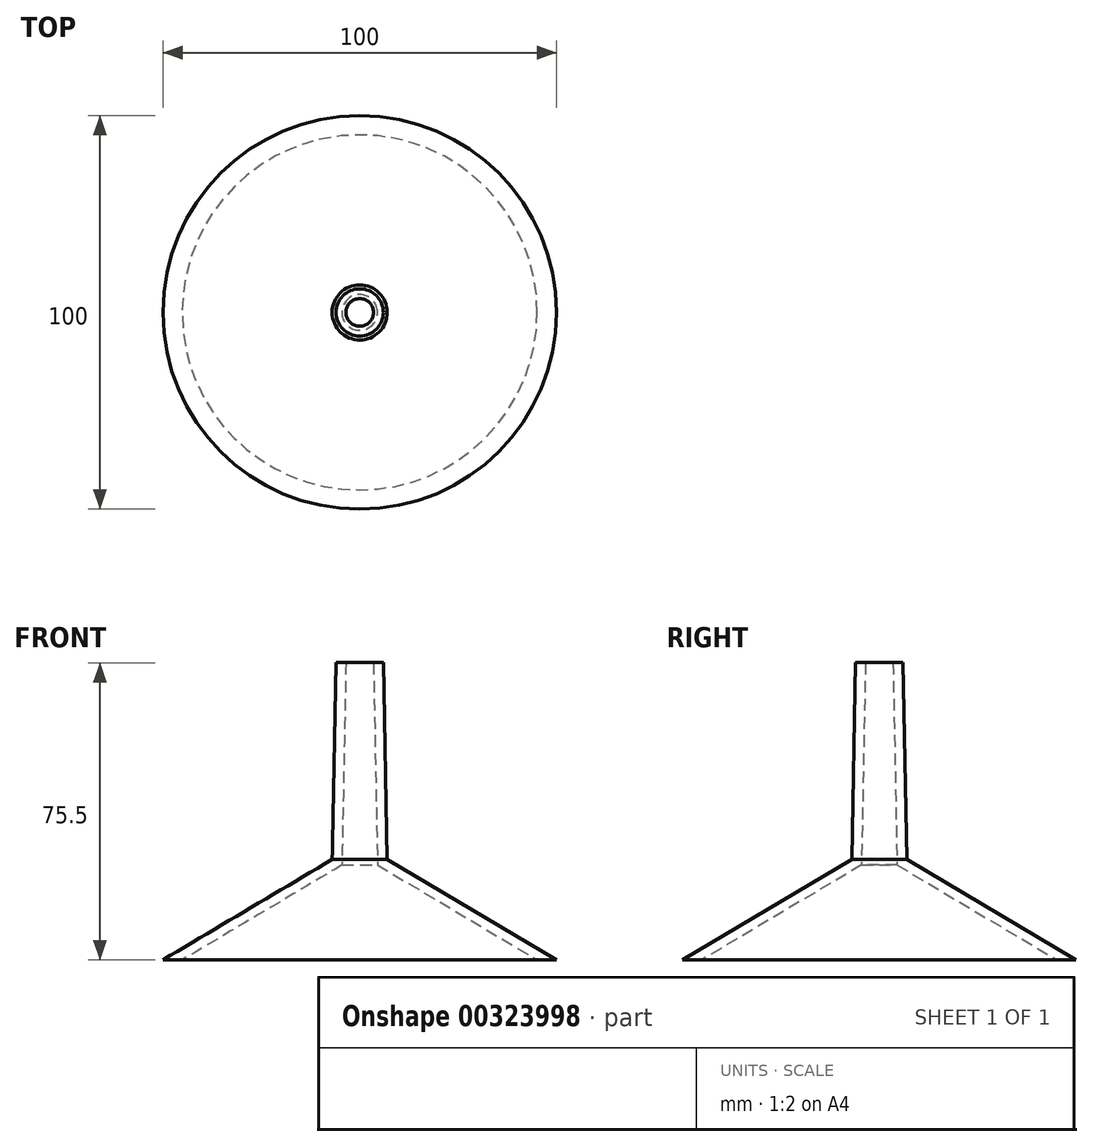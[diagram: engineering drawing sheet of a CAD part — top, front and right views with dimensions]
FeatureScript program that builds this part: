
annotation { "Feature Type Name" : "Feature", "Feature Type Description" : "" }
export const myFeature = defineFeature(function(context is Context, id is Id, definition is map)
    precondition{}
    {
        {
            var Q0;
            Q0=qCreatedBy(makeId("Front.planeOp"),FACE);
            var sketch = newSketch(context, id + "F0", { "sketchPlane" : qUnion([Q0])});
            skLineSegment(sketch, "E0", {"start": v(0, 0) * mm, "end": v(0, 75.5) * mm, "construction": true});
            skLineSegment(sketch, "E1", {"start": v(-6, 75.5) * mm, "end": v(-7, 25.51) * mm});
            skLineSegment(sketch, "E2", {"start": v(-7, 25.51) * mm, "end": v(-50, 0) * mm});
            skLineSegment(sketch, "E3.MirrorCS", {"start": v(6, 75.5) * mm, "end": v(7, 25.51) * mm});
            skLineSegment(sketch, "E4.MirrorCS", {"start": v(7, 25.51) * mm, "end": v(50, 0) * mm});
            skLineSegment(sketch, "E5.0", {"start": v(-4.53, 24.07) * mm, "end": v(-45.1, 0) * mm});
            skLineSegment(sketch, "E5.1", {"start": v(-3.5, 75.5) * mm, "end": v(-4.53, 24.07) * mm});
            skLineSegment(sketch, "E5.2", {"start": v(4.53, 24.07) * mm, "end": v(45.1, 0) * mm});
            skLineSegment(sketch, "E5.3", {"start": v(3.5, 75.5) * mm, "end": v(4.53, 24.07) * mm});
            skLineSegment(sketch, "E6", {"start": v(-50, 0) * mm, "end": v(-45.1, 0) * mm});
            skLineSegment(sketch, "E7", {"start": v(45.1, 0) * mm, "end": v(50, 0) * mm});
            skLineSegment(sketch, "E8", {"start": v(-6, 75.5) * mm, "end": v(-3.5, 75.5) * mm});
            skLineSegment(sketch, "E9", {"start": v(3.5, 75.5) * mm, "end": v(6, 75.5) * mm});
            skSolve(sketch);
        }
        {
            var Q0;
            Q0 = qSketchRegion(id + "F0", true);
            var Q1;
            Q1=sQuery(id+"F0.wireOp",EDGE,"E0");
            revolve(context, id + "F1", {"entities" : qUnion([Q0]), "axis" : qUnion([Q1]), "revolveType" : RevolveType.FULL});
        }
    });
